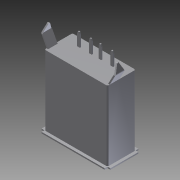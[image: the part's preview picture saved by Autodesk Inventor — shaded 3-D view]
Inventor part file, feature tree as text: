
AUTODESK INVENTOR PART (.ipt)
format: ipt  version: 2013 (Build 170138000, 138)  size: 173,568 bytes
history: native  units: mm
features: mirror x1, imported_body x1
ambient origin geometry x8: Origin, YZ Plane, XZ Plane, XY Plane, X Axis, Y Axis, Z Axis, Center Point
feature tree (2):
  mirror  "Mirror2"
  imported_body  "Base1"
